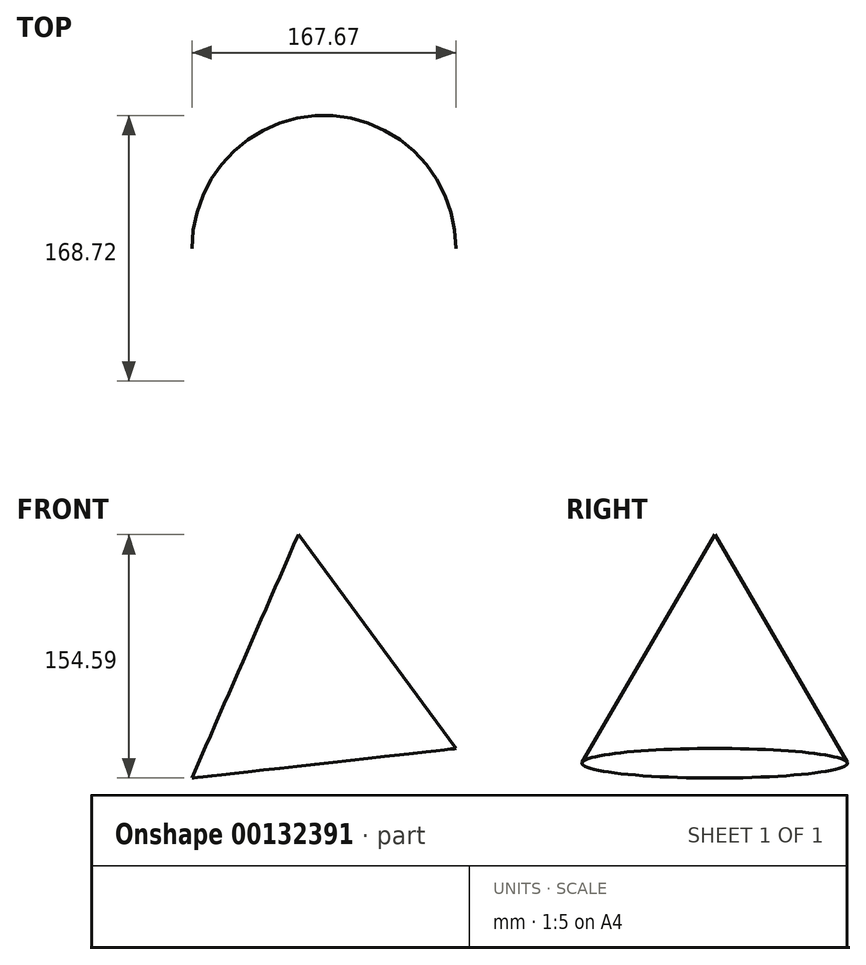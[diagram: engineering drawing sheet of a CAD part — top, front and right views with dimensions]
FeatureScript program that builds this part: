
annotation { "Feature Type Name" : "Feature", "Feature Type Description" : "" }
export const myFeature = defineFeature(function(context is Context, id is Id, definition is map)
    precondition{}
    {
        {
            var Q0;
            Q0=qCreatedBy(makeId("Front.planeOp"),FACE);
            var sketch = newSketch(context, id + "F0", { "sketchPlane" : qUnion([Q0])});
            skCircle(sketch, "E0.cCircle", {"center": v(0, 0) * mm, "radius": 48.7 * mm, "construction": true});
            skLineSegment(sketch, "E0.0", {"start": v(-10.84, 96.8) * mm, "end": v(89.26, -39.01) * mm});
            skLineSegment(sketch, "E0.1", {"start": v(89.26, -39.01) * mm, "end": v(-78.41, -57.8) * mm});
            skLineSegment(sketch, "E0.2", {"start": v(-78.41, -57.8) * mm, "end": v(-10.84, 96.8) * mm});
            skPoint(sketch, "E0.0.midPoint", {"position": v(39.2, 28.9) * mm});
            skPoint(sketch, "E1.endSnap0", {"position": v(5.42, -48.4) * mm});
            skLineSegment(sketch, "E2", {"start": v(-10.84, 96.8) * mm, "end": v(5.42, -48.4) * mm});
            skSolve(sketch);
        }
        {
            var Q0;
            {var subQ0=sQuery(id+"F0.wireOp",EDGE,"E0.2");Q0=makeQuery(id+"F0.imprint","IMPRINT",FACE,{"disambiguationData":[TD([[makeQuery(id+"F0.imprint","IMPRINT",EDGE,{"derivedFrom":subQ0}),-1.0]])]});}
            var Q1;
            Q1=sQuery(id+"F0.wireOp",EDGE,"E2");
            revolve(context, id + "F1", {"entities" : qUnion([Q0]), "axis" : qUnion([Q1]), "revolveType" : RevolveType.FULL});
        }
    });
